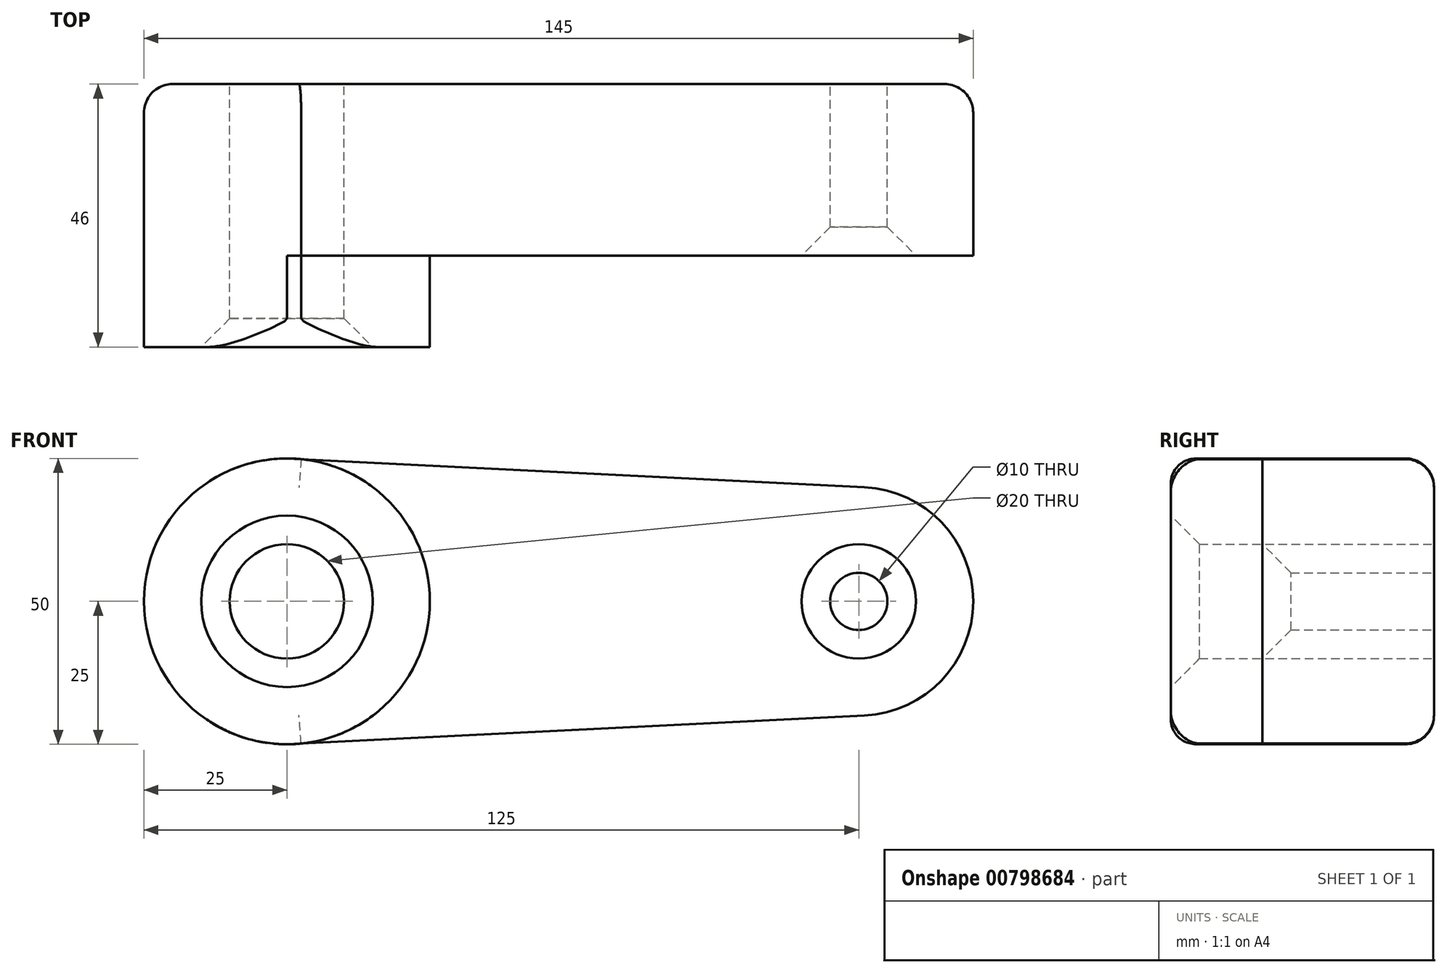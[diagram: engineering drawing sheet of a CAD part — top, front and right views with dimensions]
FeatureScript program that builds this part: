
annotation { "Feature Type Name" : "Feature", "Feature Type Description" : "" }
export const myFeature = defineFeature(function(context is Context, id is Id, definition is map)
    precondition{}
    {
        {
            var Q0;
            Q0=qCreatedBy(makeId("Front.planeOp"),FACE);
            var sketch = newSketch(context, id + "F0", { "sketchPlane" : qUnion([Q0])});
            skCircle(sketch, "E0", {"center": v(0, 0) * mm, "radius": 25 * mm});
            skCircle(sketch, "E1", {"center": v(100, 0) * mm, "radius": 20 * mm});
            skCircle(sketch, "E2", {"center": v(0, 0) * mm, "radius": 10 * mm});
            skCircle(sketch, "E3", {"center": v(100, 0) * mm, "radius": 5 * mm});
            skLineSegment(sketch, "E4", {"start": v(0, 25) * mm, "end": v(101, 19.98) * mm});
            skLineSegment(sketch, "E5", {"start": v(0, -25) * mm, "end": v(101, -19.98) * mm});
            skSolve(sketch);
        }
        {
            var Q0;
            Q0 = qSketchRegion(id + "F0", true);
            extrude(context, id + "F1", {"entities" : qUnion([Q0]), "depth" : 30 * mm, "offsetDistance" : 25 * mm});
        }
        {
            var Q0;
            Q0=makeQuery(id+"F0.imprint","IMPRINT",FACE,{"disambiguationData":[TD([[makeQuery(id+"F0.imprint","IMPRINT",EDGE,{"derivedFrom":sQuery(id+"F0.wireOp",EDGE,"E2")}),-1.0]])]});
            extrude(context, id + "F2", {"entities" : qUnion([Q0]), "operationType" : NewBodyOperationType.ADD, "depth" : 25 * mm, "offsetDistance" : 25 * mm});
        }
        {
            var Q0;
            Q0=makeQuery(id+"F0.imprint","IMPRINT",FACE,{"disambiguationData":[TD([[makeQuery(id+"F0.imprint","IMPRINT",EDGE,{"derivedFrom":sQuery(id+"F0.wireOp",EDGE,"E2")}),-1.0]])]});
            extrude(context, id + "F3", {"entities" : qUnion([Q0]), "operationType" : NewBodyOperationType.ADD, "depth" : 46 * mm, "offsetDistance" : 25 * mm});
        }
        {
            var Q0;
            Q0=makeQuery(id+"F1.opExtrude","CAP_EDGE",EDGE,{"disambiguationData":[OSD([sQuery(id+"F0.wireOp",EDGE,"E5")])],"isStart":true});
            var Q1;
            {var subQ0=sQuery(id+"F0.wireOp",EDGE,"E0");Q1=makeQuery(id+"F3.opExtrude","CAP_EDGE",EDGE,{"disambiguationData":[OSD([subQ0]),TDD([makeQuery(id+"F0.imprint","IMPRINT",EDGE,{"disambiguationData":[TD([[makeQuery(id+"F0.imprint","INTERSECT",VERTEX,{"disambiguationData":[OD(1.0)],"derivedFrom":[subQ0,sQuery(id+"F0.wireOp",EDGE,"E4")]}),1.0]])],"derivedFrom":subQ0})])],"isStart":false});}
            var Q2;
            {var subQ0=sQuery(id+"F0.wireOp",EDGE,"E0");Q2=makeQuery(id+"F3.opExtrude","CAP_EDGE",EDGE,{"disambiguationData":[OSD([subQ0]),TDD([makeQuery(id+"F0.imprint","IMPRINT",EDGE,{"disambiguationData":[TD([[makeQuery(id+"F0.imprint","INTERSECT",VERTEX,{"disambiguationData":[OD(0.0)],"derivedFrom":[subQ0,sQuery(id+"F0.wireOp",EDGE,"E4")]}),-1.0]])],"derivedFrom":subQ0})])],"isStart":false});}
            var Q3;
            Q3=makeQuery(id+"F3.opExtrude","CAP_EDGE",EDGE,{"disambiguationData":[OSD([sQuery(id+"F0.wireOp",EDGE,"E5")])],"isStart":false});
            var Q4;
            Q4=makeQuery(id+"F3.opExtrude","CAP_EDGE",EDGE,{"disambiguationData":[OSD([sQuery(id+"F0.wireOp",EDGE,"E4")])],"isStart":false});
            fillet(context, id + "F4", {"entities" : qUnion([Q0, Q1, Q2, Q3, Q4]), "radius" : 5 * mm, "tangentPropagation" : true, "allowEdgeOverflow" : false});
        }
        {
            var Q0;
            Q0=makeQuery(id+"F3.opExtrude","CAP_EDGE",EDGE,{"disambiguationData":[OSD([sQuery(id+"F0.wireOp",EDGE,"E2")])],"isStart":false});
            var Q1;
            Q1=makeQuery(id+"F1.opExtrude","CAP_EDGE",EDGE,{"disambiguationData":[OSD([sQuery(id+"F0.wireOp",EDGE,"E3")])],"isStart":false});
            chamfer(context, id + "F5", {"entities" : qUnion([Q0, Q1]), "width" : 5 * mm, "tangentPropagation" : true});
        }
        {
            var Q0;
            Q0=makeQuery(id+"F1.opExtrude","CAP_EDGE",EDGE,{"disambiguationData":[OSD([sQuery(id+"F0.wireOp",EDGE,"E0")])],"isStart":true});
            fillet(context, id + "F6", {"entities" : qUnion([Q0]), "radius" : 5 * mm, "tangentPropagation" : true, "allowEdgeOverflow" : false});
        }
    });
